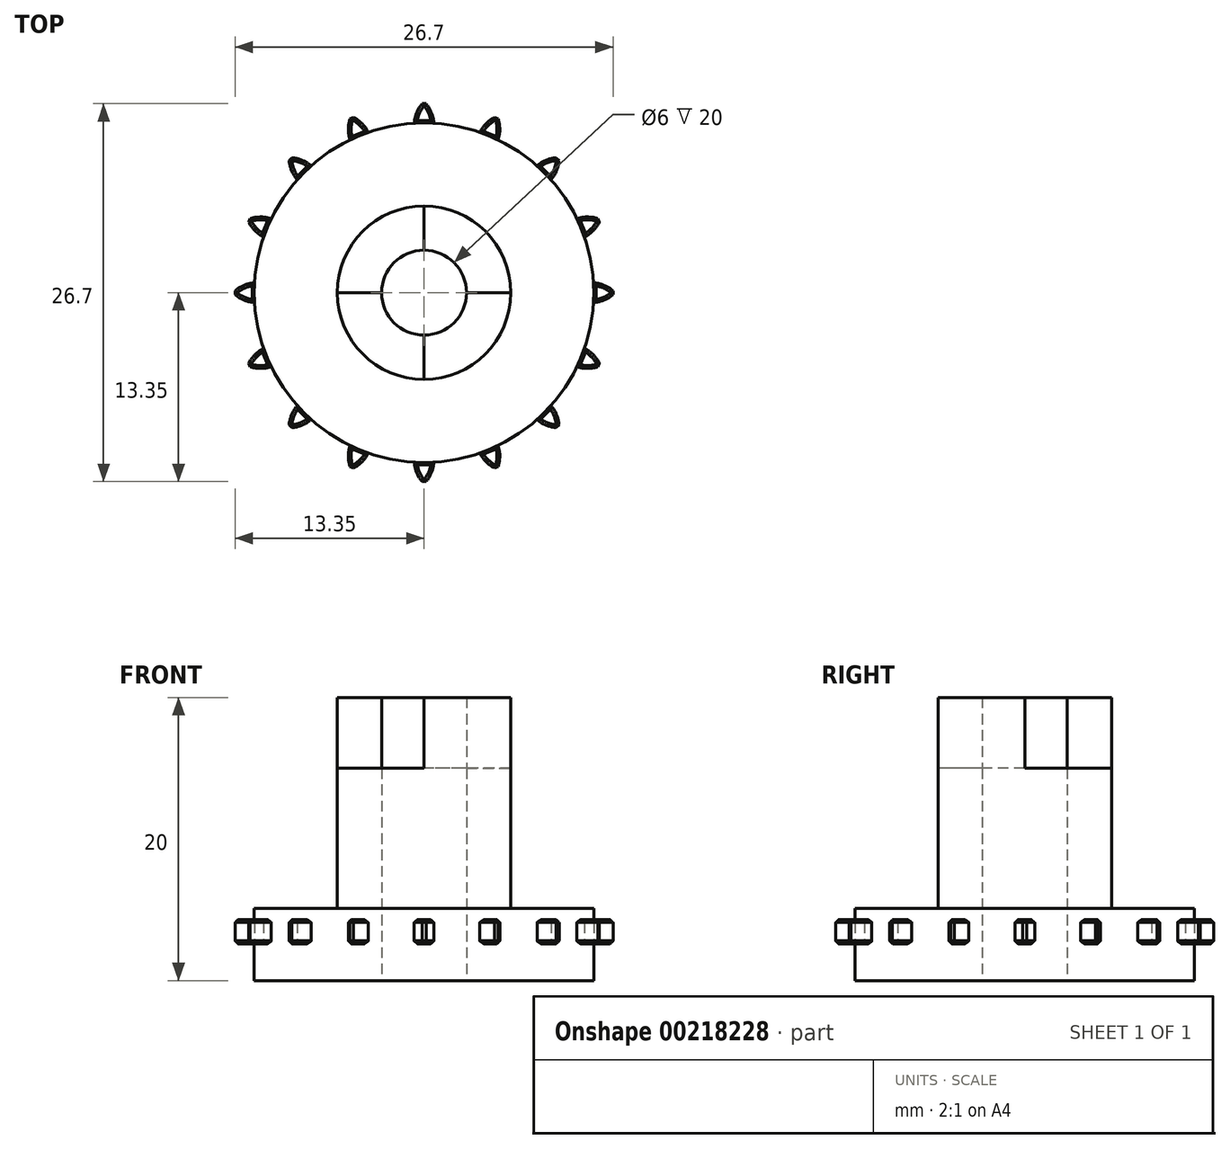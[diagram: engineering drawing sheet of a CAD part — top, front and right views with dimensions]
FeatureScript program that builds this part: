
annotation { "Feature Type Name" : "Feature", "Feature Type Description" : "" }
export const myFeature = defineFeature(function(context is Context, id is Id, definition is map)
    precondition{}
    {
        {
            var Q0;
            Q0=qCreatedBy(makeId("Top.planeOp"),FACE);
            var sketch = newSketch(context, id + "F0", { "sketchPlane" : qUnion([Q0])});
            skCircle(sketch, "E0", {"center": v(0, 0) * mm, "radius": 12 * mm});
            skLineSegment(sketch, "E1", {"start": v(0, 0) * mm, "end": v(12, 0) * mm});
            skSolve(sketch);
        }
        {
            var Q0;
            Q0=makeQuery(id+"F0.imprint","IMPRINT",FACE,{"disambiguationData":[TD([[makeQuery(id+"F0.imprint","IMPRINT",EDGE,{"derivedFrom":sQuery(id+"F0.wireOp",EDGE,"E0")}),1.0]])]});
            extrude(context, id + "F1", {"entities" : qUnion([Q0]), "depth" : 5.1 * mm});
        }
        {
            var Q0;
            Q0=qCreatedBy(makeId("Top.planeOp"),FACE);
            cPlane(context, id + "F2", {"entities" : qUnion([Q0]), "cplaneType" : CPlaneType.OFFSET, "offset" : 2.6 * mm, "width" : 150 * mm, "height" : 150 * mm});
        }
        {
            var Q0;
            Q0=qCreatedBy(id+"F2.planeOp",FACE);
            var sketch = newSketch(context, id + "F3", { "sketchPlane" : qUnion([Q0])});
            skLineSegment(sketch, "E2", {"start": v(-3.73, 12) * mm, "end": v(8.98, 12) * mm, "construction": true});
            skLineSegment(sketch, "E3", {"start": v(-2.65, 11.8) * mm, "end": v(3.22, 11.8) * mm, "construction": true});
            skCircle(sketch, "E4", {"center": v(-1.7, 11.8) * mm, "radius": 2.4 * mm, "construction": true});
            skLineSegment(sketch, "E5", {"start": v(-3.15, 13.35) * mm, "end": v(2.93, 13.35) * mm, "construction": true});
            skLineSegment(sketch, "E6", {"start": v(0.7, 13.77) * mm, "end": v(0.7, 11.3) * mm, "construction": true});
            skLineSegment(sketch, "E7.MirrorCS", {"start": v(3.15, 13.35) * mm, "end": v(-2.93, 13.35) * mm, "construction": true});
            skLineSegment(sketch, "E8", {"start": v(0, 13.35) * mm, "end": v(0.14, 13.35) * mm});
            skFitSpline(sketch, "E9", {"points": [v(0.14, 13.35) * mm, v(0.3, 13.13) * mm, v(0.53, 12.69) * mm, v(0.65, 12.33) * mm, v(0.7, 11.95) * mm], "startDerivative": vector(0.73, -0.9) * mm, "endDerivative": vector(0.2, -1.49) * mm});
            skFitSpline(sketch, "E10.MirrorCS", {"points": [v(-0.14, 13.35) * mm, v(-0.3, 13.13) * mm, v(-0.53, 12.69) * mm, v(-0.65, 12.33) * mm, v(-0.7, 11.95) * mm], "startDerivative": vector(-0.73, -0.9) * mm, "endDerivative": vector(-0.2, -1.49) * mm});
            skLineSegment(sketch, "E11", {"start": v(-0.7, 11.95) * mm, "end": v(0.7, 11.95) * mm});
            skLineSegment(sketch, "E12", {"start": v(-0.14, 13.35) * mm, "end": v(0.14, 13.35) * mm});
            skSolve(sketch);
        }
        {
            var Q0;
            {var subQ0=sQuery(id+"F3.wireOp",EDGE,"E9");Q0=makeQuery(id+"F3.imprint","IMPRINT",FACE,{"disambiguationData":[TD([[makeQuery(id+"F3.imprint","IMPRINT",EDGE,{"derivedFrom":subQ0}),-1.0]])]});}
            extrude(context, id + "F4", {"entities" : qUnion([Q0]), "depth" : 1.7 * mm});
        }
        {
            var Q0;
            Q0=makeQuery(id+"F4.opExtrude","CAP_FACE",FACE,{"disambiguationData":[OSD([sQuery(id+"F3.wireOp",EDGE,"E9"),sQuery(id+"F3.wireOp",EDGE,"E10.MirrorCS"),sQuery(id+"F3.wireOp",EDGE,"E11"),sQuery(id+"F3.wireOp",EDGE,"E12")])],"isStart":true});
            var Q1;
            Q1=makeQuery(id+"F4.opExtrude","CAP_FACE",FACE,{"disambiguationData":[OSD([sQuery(id+"F3.wireOp",EDGE,"E9"),sQuery(id+"F3.wireOp",EDGE,"E10.MirrorCS"),sQuery(id+"F3.wireOp",EDGE,"E11"),sQuery(id+"F3.wireOp",EDGE,"E12")])],"isStart":false});
            chamfer(context, id + "F5", {"entities" : qUnion([Q0, Q1]), "width" : 0.2 * mm, "tangentPropagation" : true});
        }
        {
            var Q0;
            Q0=makeQuery(id+"F4.opExtrude","SWEPT_BODY",BODY,{"disambiguationData":[OSD([sQuery(id+"F3.wireOp",EDGE,"E9"),sQuery(id+"F3.wireOp",EDGE,"E10.MirrorCS"),sQuery(id+"F3.wireOp",EDGE,"E11"),sQuery(id+"F3.wireOp",EDGE,"E12")])]});
            var Q1;
            Q1=makeQuery(id+"F1.opExtrude","CAP_EDGE",EDGE,{"disambiguationData":[OSD([sQuery(id+"F0.wireOp",EDGE,"E0")])],"isStart":true});
            circularPattern(context, id + "F6", {"operationType" : NewBodyOperationType.ADD, "entities" : qUnion([Q0]), "axis" : qUnion([Q1]), "angle" : 360 * degree, "instanceCount" : 16, "equalSpace" : true});
        }
        {
            var Q0;
            Q0=makeQuery(id+"F1.opExtrude","CAP_FACE",FACE,{"disambiguationData":[OSD([sQuery(id+"F0.wireOp",EDGE,"E0")])],"isStart":false});
            var sketch = newSketch(context, id + "F7", { "sketchPlane" : qUnion([Q0])});
            skCircle(sketch, "E13", {"center": v(0, 0) * mm, "radius": 6.13 * mm});
            skSolve(sketch);
        }
        {
            var Q0;
            Q0 = qSketchRegion(id + "F7", true);
            extrude(context, id + "F8", {"entities" : qUnion([Q0]), "operationType" : NewBodyOperationType.ADD, "depth" : 14.9 * mm});
        }
        {
            var Q0;
            Q0=sQuery(id+"F0.wireOp",VERTEX,"E0.center");
            var Q1;
            Q1=makeQuery(id+"F1.opExtrude","SWEPT_BODY",BODY,{"disambiguationData":[OSD([sQuery(id+"F0.wireOp",EDGE,"E0")])]});
            hole(context, id + "F9", {"style" : HoleStyle.SIMPLE, "endStyle" : HoleEndStyle.THROUGH, "oppositeDirection" : true, "holeDiameter" : 6 * mm, "locations" : qUnion([Q0]), "scope" : qUnion([Q1]), "isTappedThrough" : true});
        }
        {
            var Q0;
            Q0=makeQuery(id+"F8.opExtrude","CAP_FACE",FACE,{"disambiguationData":[OSD([sQuery(id+"F7.wireOp",EDGE,"E13")])],"isStart":false});
            var sketch = newSketch(context, id + "F10", { "sketchPlane" : qUnion([Q0])});
            skLineSegment(sketch, "E14", {"start": v(-13.72, 0) * mm, "end": v(13.52, 0) * mm});
            skLineSegment(sketch, "E15", {"start": v(13.52, 0) * mm, "end": v(13.52, 13.6) * mm});
            skLineSegment(sketch, "E16", {"start": v(13.52, 13.6) * mm, "end": v(0, 13.6) * mm});
            skLineSegment(sketch, "E17", {"start": v(0, 13.6) * mm, "end": v(0, -13.98) * mm});
            skLineSegment(sketch, "E18", {"start": v(0, -13.98) * mm, "end": v(-13.72, -13.98) * mm});
            skLineSegment(sketch, "E19", {"start": v(-13.72, -13.98) * mm, "end": v(-13.72, 0) * mm});
            skSolve(sketch);
        }
        {
            var Q0;
            Q0 = qSketchRegion(id + "F10", true);
            extrude(context, id + "F11", {"entities" : qUnion([Q0]), "operationType" : NewBodyOperationType.REMOVE, "oppositeDirection" : true, "depth" : 5 * mm});
        }
    });
